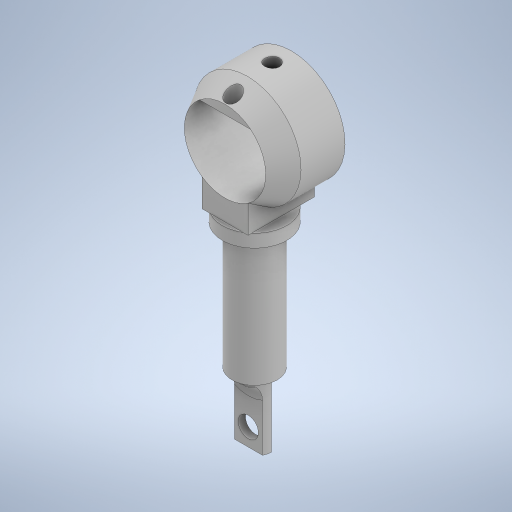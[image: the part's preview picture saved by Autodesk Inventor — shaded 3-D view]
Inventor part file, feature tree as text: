
AUTODESK INVENTOR PART (.ipt)
format: ipt  version: 2023 (Build 270158030, 158C)  size: 431,616 bytes
history: mixed  units: in
note: dims shown in document units (in); Inventor stores cm internally (conversion verified against a paired STEP export)
features: other x6, move_body x2, chamfer x1, direct_edit x1, imported_body x1
ambient origin geometry x8: Origin, YZ Plane, XZ Plane, XY Plane, X Axis, Y Axis, Z Axis, Center Point
bodies: Solid1 (imported_parasolid), Solid4 (imported_parasolid), Solid6 (imported_parasolid), Solid10 (imported_parasolid), Solid23 (imported_parasolid), Solid37 (imported_parasolid)
feature tree (11):
  other  "MouseEarbar"
  chamfer  "Chamfer1"  Distance=0.1181in Angle=60.0deg
  direct_edit  "Direct Edit1"
  other  "Rat_ToothHolder"
  other  "Mouse_ToothHolder"
  other  "MouseNoseCone"
  other  "RatNoseCone"
  other  "RatEarbar_1"
  move_body  "Move1"
  move_body  "Move2"
  imported_body  NMx_Import_Brep_tag  [imported B-rep: ~8 faces, bbox_mm=[5.050483, 0.0, 0.0]]
